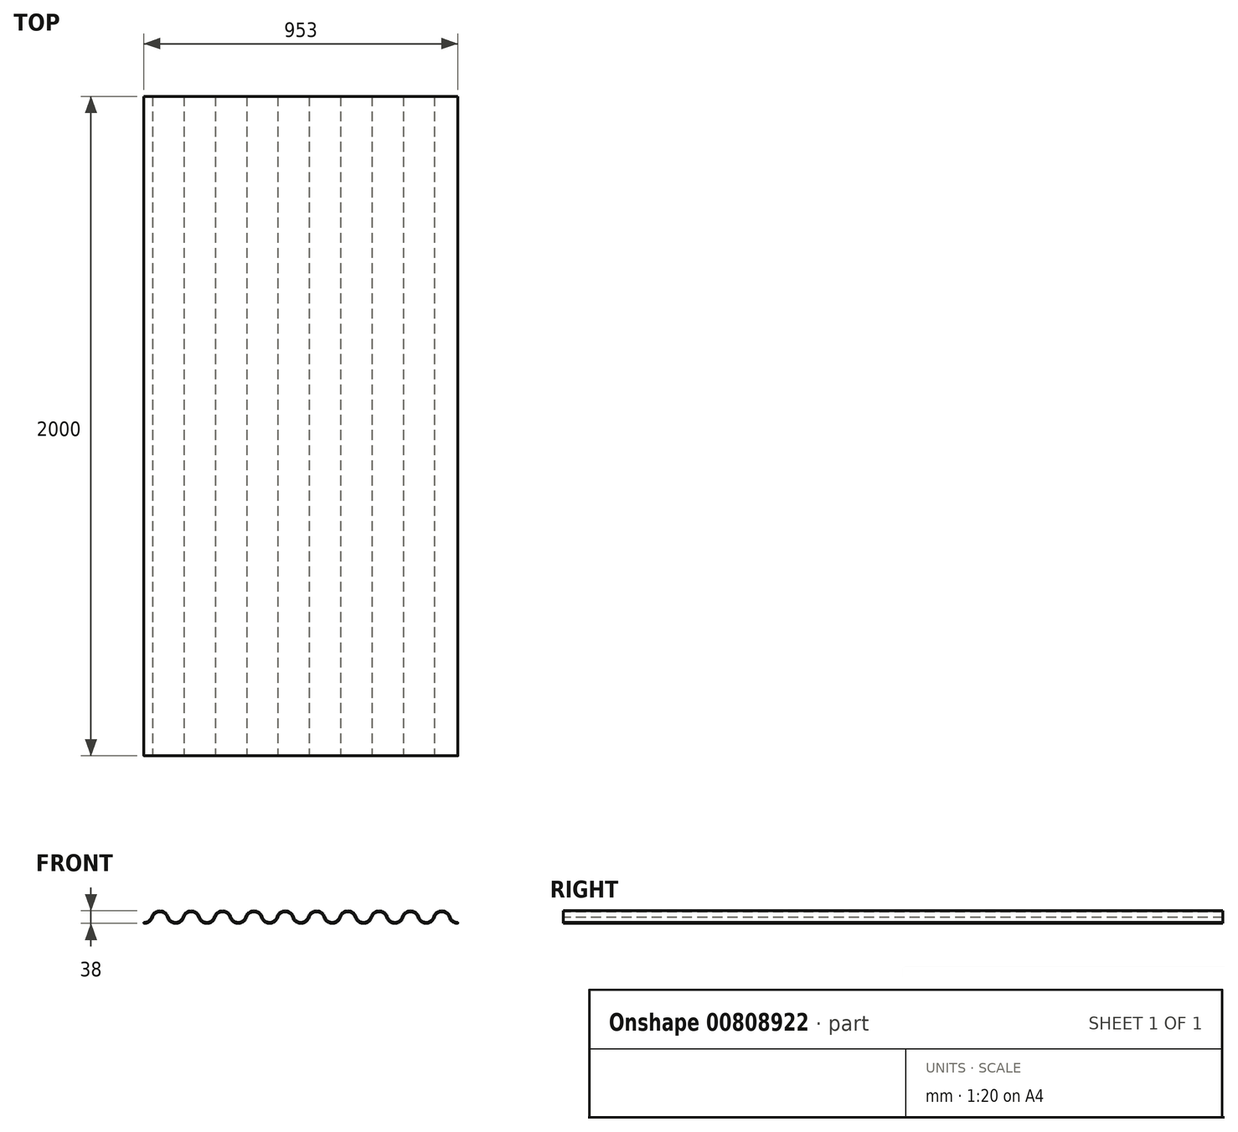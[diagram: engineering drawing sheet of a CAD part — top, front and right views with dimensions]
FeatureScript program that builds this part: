
annotation { "Feature Type Name" : "Feature", "Feature Type Description" : "" }
export const myFeature = defineFeature(function(context is Context, id is Id, definition is map)
    precondition{}
    {
        {
            var Q0;
            Q0=qCreatedBy(makeId("Front.planeOp"),FACE);
            var sketch = newSketch(context, id + "F0", { "sketchPlane" : qUnion([Q0])});
            skPoint(sketch, "E0.middle", {"position": v(0, 0) * mm});
            skArc(sketch, "E1", {"start": v(-47.5, -17.5) * mm, "mid": v(-32.61, -12.55) * mm, "end": v(-23.65, 0.32) * mm});
            skArc(sketch, "E2", {"start": v(0, 17.5) * mm, "mid": v(-14.62, 12.75) * mm, "end": v(-23.65, 0.32) * mm});
            skArc(sketch, "E3", {"start": v(23.75, 0) * mm, "mid": v(14.76, 12.66) * mm, "end": v(0, 17.5) * mm});
            skArc(sketch, "E4", {"start": v(23.75, 0) * mm, "mid": v(32.75, -12.65) * mm, "end": v(47.5, -17.5) * mm});
            skArc(sketch, "E5.0.startCap", {"start": v(-47.5, -19) * mm, "mid": v(-49, -17.5) * mm, "end": v(-47.5, -16) * mm});
            skArc(sketch, "E5.0.endCap", {"start": v(-25.1, 0.75) * mm, "mid": v(-23.23, 1.76) * mm, "end": v(-22.21, -0.1) * mm});
            skArc(sketch, "E5.0.left", {"start": v(-47.5, -16) * mm, "mid": v(-33.51, -11.35) * mm, "end": v(-25.1, 0.75) * mm});
            skArc(sketch, "E5.0.right", {"start": v(-47.5, -19) * mm, "mid": v(-31.72, -13.75) * mm, "end": v(-22.21, -0.1) * mm});
            skArc(sketch, "E5.1.startCap", {"start": v(0, 19) * mm, "mid": v(1.5, 17.5) * mm, "end": v(0, 16) * mm});
            skArc(sketch, "E5.1.endCap", {"start": v(-22.23, -0.14) * mm, "mid": v(-24.12, -1.1) * mm, "end": v(-25.08, 0.79) * mm});
            skArc(sketch, "E5.1.left", {"start": v(0, 16) * mm, "mid": v(-13.73, 11.54) * mm, "end": v(-22.23, -0.14) * mm});
            skArc(sketch, "E5.1.right", {"start": v(0, 19) * mm, "mid": v(-15.5, 13.97) * mm, "end": v(-25.08, 0.79) * mm});
            skArc(sketch, "E5.2.startCap", {"start": v(25.18, 0.44) * mm, "mid": v(24.2, -1.43) * mm, "end": v(22.32, -0.44) * mm});
            skArc(sketch, "E5.2.endCap", {"start": v(0, 16) * mm, "mid": v(-1.5, 17.5) * mm, "end": v(0, 19) * mm});
            skArc(sketch, "E5.2.left", {"start": v(22.32, -0.44) * mm, "mid": v(13.87, 11.46) * mm, "end": v(0, 16) * mm});
            skArc(sketch, "E5.2.right", {"start": v(25.18, 0.44) * mm, "mid": v(15.65, 13.87) * mm, "end": v(0, 19) * mm});
            skArc(sketch, "E5.3.startCap", {"start": v(22.32, -0.44) * mm, "mid": v(23.3, 1.43) * mm, "end": v(25.18, 0.44) * mm});
            skArc(sketch, "E5.3.endCap", {"start": v(47.5, -16) * mm, "mid": v(49, -17.5) * mm, "end": v(47.5, -19) * mm});
            skArc(sketch, "E5.3.left", {"start": v(25.18, 0.44) * mm, "mid": v(33.64, -11.44) * mm, "end": v(47.5, -16) * mm});
            skArc(sketch, "E5.3.right", {"start": v(22.32, -0.44) * mm, "mid": v(31.86, -13.86) * mm, "end": v(47.5, -19) * mm});
            skArc(sketch, "E6.1.0.0", {"start": v(47.5, -19) * mm, "mid": v(63.28, -13.75) * mm, "end": v(72.79, -0.1) * mm});
            skArc(sketch, "E6.1.0.1", {"start": v(95, 19) * mm, "mid": v(79.5, 13.97) * mm, "end": v(69.92, 0.79) * mm});
            skArc(sketch, "E6.1.0.2", {"start": v(118.75, 0) * mm, "mid": v(109.76, 12.66) * mm, "end": v(95, 17.5) * mm});
            skArc(sketch, "E6.1.0.3", {"start": v(72.77, -0.14) * mm, "mid": v(70.88, -1.1) * mm, "end": v(69.92, 0.79) * mm});
            skArc(sketch, "E6.1.0.4", {"start": v(47.5, -17.5) * mm, "mid": v(62.39, -12.55) * mm, "end": v(71.35, 0.32) * mm});
            skArc(sketch, "E6.1.0.5", {"start": v(118.75, 0) * mm, "mid": v(127.75, -12.65) * mm, "end": v(142.5, -17.5) * mm});
            skArc(sketch, "E6.1.0.6", {"start": v(95, 17.5) * mm, "mid": v(80.38, 12.75) * mm, "end": v(71.35, 0.32) * mm});
            skPoint(sketch, "E6.1.0.7", {"position": v(95, 0) * mm});
            skArc(sketch, "E6.1.0.8", {"start": v(95, 16) * mm, "mid": v(81.27, 11.54) * mm, "end": v(72.77, -0.14) * mm});
            skArc(sketch, "E6.1.0.9", {"start": v(117.32, -0.44) * mm, "mid": v(108.87, 11.46) * mm, "end": v(95, 16) * mm});
            skArc(sketch, "E6.1.0.10", {"start": v(120.18, 0.44) * mm, "mid": v(128.64, -11.44) * mm, "end": v(142.5, -16) * mm});
            skArc(sketch, "E6.1.0.11", {"start": v(95, 19) * mm, "mid": v(96.5, 17.5) * mm, "end": v(95, 16) * mm});
            skArc(sketch, "E6.1.0.12", {"start": v(47.5, -16) * mm, "mid": v(61.49, -11.35) * mm, "end": v(69.9, 0.75) * mm});
            skArc(sketch, "E6.1.0.13", {"start": v(117.32, -0.44) * mm, "mid": v(126.86, -13.86) * mm, "end": v(142.5, -19) * mm});
            skArc(sketch, "E6.1.0.14", {"start": v(120.18, 0.44) * mm, "mid": v(119.2, -1.43) * mm, "end": v(117.32, -0.44) * mm});
            skArc(sketch, "E6.1.0.15", {"start": v(47.5, -19) * mm, "mid": v(46, -17.5) * mm, "end": v(47.5, -16) * mm});
            skArc(sketch, "E6.1.0.16", {"start": v(69.9, 0.75) * mm, "mid": v(71.77, 1.76) * mm, "end": v(72.79, -0.1) * mm});
            skArc(sketch, "E6.1.0.17", {"start": v(142.5, -16) * mm, "mid": v(144, -17.5) * mm, "end": v(142.5, -19) * mm});
            skArc(sketch, "E6.1.0.18", {"start": v(120.18, 0.44) * mm, "mid": v(110.65, 13.87) * mm, "end": v(95, 19) * mm});
            skArc(sketch, "E6.1.0.19", {"start": v(117.32, -0.44) * mm, "mid": v(118.3, 1.43) * mm, "end": v(120.18, 0.44) * mm});
            skArc(sketch, "E6.1.0.20", {"start": v(95, 16) * mm, "mid": v(93.5, 17.5) * mm, "end": v(95, 19) * mm});
            skArc(sketch, "E6.2.0.0", {"start": v(142.5, -19) * mm, "mid": v(158.28, -13.75) * mm, "end": v(167.79, -0.1) * mm});
            skArc(sketch, "E6.2.0.1", {"start": v(190, 19) * mm, "mid": v(174.5, 13.97) * mm, "end": v(164.92, 0.79) * mm});
            skArc(sketch, "E6.2.0.2", {"start": v(213.75, 0) * mm, "mid": v(204.76, 12.66) * mm, "end": v(190, 17.5) * mm});
            skArc(sketch, "E6.2.0.3", {"start": v(167.77, -0.14) * mm, "mid": v(165.88, -1.1) * mm, "end": v(164.92, 0.79) * mm});
            skArc(sketch, "E6.2.0.4", {"start": v(142.5, -17.5) * mm, "mid": v(157.39, -12.55) * mm, "end": v(166.35, 0.32) * mm});
            skArc(sketch, "E6.2.0.5", {"start": v(213.75, 0) * mm, "mid": v(222.75, -12.65) * mm, "end": v(237.5, -17.5) * mm});
            skArc(sketch, "E6.2.0.6", {"start": v(190, 17.5) * mm, "mid": v(175.38, 12.75) * mm, "end": v(166.35, 0.32) * mm});
            skPoint(sketch, "E6.2.0.7", {"position": v(190, 0) * mm});
            skArc(sketch, "E6.2.0.8", {"start": v(190, 16) * mm, "mid": v(176.27, 11.54) * mm, "end": v(167.77, -0.14) * mm});
            skArc(sketch, "E6.2.0.9", {"start": v(212.32, -0.44) * mm, "mid": v(203.87, 11.46) * mm, "end": v(190, 16) * mm});
            skArc(sketch, "E6.2.0.10", {"start": v(215.18, 0.44) * mm, "mid": v(223.64, -11.44) * mm, "end": v(237.5, -16) * mm});
            skArc(sketch, "E6.2.0.11", {"start": v(190, 19) * mm, "mid": v(191.5, 17.5) * mm, "end": v(190, 16) * mm});
            skArc(sketch, "E6.2.0.12", {"start": v(142.5, -16) * mm, "mid": v(156.49, -11.35) * mm, "end": v(164.9, 0.75) * mm});
            skArc(sketch, "E6.2.0.13", {"start": v(212.32, -0.44) * mm, "mid": v(221.86, -13.86) * mm, "end": v(237.5, -19) * mm});
            skArc(sketch, "E6.2.0.14", {"start": v(215.18, 0.44) * mm, "mid": v(214.2, -1.43) * mm, "end": v(212.32, -0.44) * mm});
            skArc(sketch, "E6.2.0.15", {"start": v(142.5, -19) * mm, "mid": v(141, -17.5) * mm, "end": v(142.5, -16) * mm});
            skArc(sketch, "E6.2.0.16", {"start": v(164.9, 0.75) * mm, "mid": v(166.77, 1.76) * mm, "end": v(167.79, -0.1) * mm});
            skArc(sketch, "E6.2.0.17", {"start": v(237.5, -16) * mm, "mid": v(239, -17.5) * mm, "end": v(237.5, -19) * mm});
            skArc(sketch, "E6.2.0.18", {"start": v(215.18, 0.44) * mm, "mid": v(205.65, 13.87) * mm, "end": v(190, 19) * mm});
            skArc(sketch, "E6.2.0.19", {"start": v(212.32, -0.44) * mm, "mid": v(213.3, 1.43) * mm, "end": v(215.18, 0.44) * mm});
            skArc(sketch, "E6.2.0.20", {"start": v(190, 16) * mm, "mid": v(188.5, 17.5) * mm, "end": v(190, 19) * mm});
            skArc(sketch, "E6.3.0.0", {"start": v(237.5, -19) * mm, "mid": v(253.28, -13.75) * mm, "end": v(262.79, -0.1) * mm});
            skArc(sketch, "E6.3.0.1", {"start": v(285, 19) * mm, "mid": v(269.5, 13.97) * mm, "end": v(259.92, 0.79) * mm});
            skArc(sketch, "E6.3.0.2", {"start": v(308.75, 0) * mm, "mid": v(299.76, 12.66) * mm, "end": v(285, 17.5) * mm});
            skArc(sketch, "E6.3.0.3", {"start": v(262.77, -0.14) * mm, "mid": v(260.88, -1.1) * mm, "end": v(259.92, 0.79) * mm});
            skArc(sketch, "E6.3.0.4", {"start": v(237.5, -17.5) * mm, "mid": v(252.39, -12.55) * mm, "end": v(261.35, 0.32) * mm});
            skArc(sketch, "E6.3.0.5", {"start": v(308.75, 0) * mm, "mid": v(317.75, -12.65) * mm, "end": v(332.5, -17.5) * mm});
            skArc(sketch, "E6.3.0.6", {"start": v(285, 17.5) * mm, "mid": v(270.38, 12.75) * mm, "end": v(261.35, 0.32) * mm});
            skPoint(sketch, "E6.3.0.7", {"position": v(285, 0) * mm});
            skArc(sketch, "E6.3.0.8", {"start": v(285, 16) * mm, "mid": v(271.27, 11.54) * mm, "end": v(262.77, -0.14) * mm});
            skArc(sketch, "E6.3.0.9", {"start": v(307.32, -0.44) * mm, "mid": v(298.87, 11.46) * mm, "end": v(285, 16) * mm});
            skArc(sketch, "E6.3.0.10", {"start": v(310.18, 0.44) * mm, "mid": v(318.64, -11.44) * mm, "end": v(332.5, -16) * mm});
            skArc(sketch, "E6.3.0.11", {"start": v(285, 19) * mm, "mid": v(286.5, 17.5) * mm, "end": v(285, 16) * mm});
            skArc(sketch, "E6.3.0.12", {"start": v(237.5, -16) * mm, "mid": v(251.49, -11.35) * mm, "end": v(259.9, 0.75) * mm});
            skArc(sketch, "E6.3.0.13", {"start": v(307.32, -0.44) * mm, "mid": v(316.86, -13.86) * mm, "end": v(332.5, -19) * mm});
            skArc(sketch, "E6.3.0.14", {"start": v(310.18, 0.44) * mm, "mid": v(309.2, -1.43) * mm, "end": v(307.32, -0.44) * mm});
            skArc(sketch, "E6.3.0.15", {"start": v(237.5, -19) * mm, "mid": v(236, -17.5) * mm, "end": v(237.5, -16) * mm});
            skArc(sketch, "E6.3.0.16", {"start": v(259.9, 0.75) * mm, "mid": v(261.77, 1.76) * mm, "end": v(262.79, -0.1) * mm});
            skArc(sketch, "E6.3.0.17", {"start": v(332.5, -16) * mm, "mid": v(334, -17.5) * mm, "end": v(332.5, -19) * mm});
            skArc(sketch, "E6.3.0.18", {"start": v(310.18, 0.44) * mm, "mid": v(300.65, 13.87) * mm, "end": v(285, 19) * mm});
            skArc(sketch, "E6.3.0.19", {"start": v(307.32, -0.44) * mm, "mid": v(308.3, 1.43) * mm, "end": v(310.18, 0.44) * mm});
            skArc(sketch, "E6.3.0.20", {"start": v(285, 16) * mm, "mid": v(283.5, 17.5) * mm, "end": v(285, 19) * mm});
            skArc(sketch, "E6.4.0.0", {"start": v(332.5, -19) * mm, "mid": v(348.28, -13.75) * mm, "end": v(357.79, -0.1) * mm});
            skArc(sketch, "E6.4.0.1", {"start": v(380, 19) * mm, "mid": v(364.5, 13.97) * mm, "end": v(354.92, 0.79) * mm});
            skArc(sketch, "E6.4.0.2", {"start": v(403.75, 0) * mm, "mid": v(394.76, 12.66) * mm, "end": v(380, 17.5) * mm});
            skArc(sketch, "E6.4.0.3", {"start": v(357.77, -0.14) * mm, "mid": v(355.88, -1.1) * mm, "end": v(354.92, 0.79) * mm});
            skArc(sketch, "E6.4.0.4", {"start": v(332.5, -17.5) * mm, "mid": v(347.39, -12.55) * mm, "end": v(356.35, 0.32) * mm});
            skArc(sketch, "E6.4.0.5", {"start": v(403.75, 0) * mm, "mid": v(412.75, -12.65) * mm, "end": v(427.5, -17.5) * mm});
            skArc(sketch, "E6.4.0.6", {"start": v(380, 17.5) * mm, "mid": v(365.38, 12.75) * mm, "end": v(356.35, 0.32) * mm});
            skPoint(sketch, "E6.4.0.7", {"position": v(380, 0) * mm});
            skArc(sketch, "E6.4.0.8", {"start": v(380, 16) * mm, "mid": v(366.27, 11.54) * mm, "end": v(357.77, -0.14) * mm});
            skArc(sketch, "E6.4.0.9", {"start": v(402.32, -0.44) * mm, "mid": v(393.87, 11.46) * mm, "end": v(380, 16) * mm});
            skArc(sketch, "E6.4.0.10", {"start": v(405.18, 0.44) * mm, "mid": v(413.64, -11.44) * mm, "end": v(427.5, -16) * mm});
            skArc(sketch, "E6.4.0.11", {"start": v(380, 19) * mm, "mid": v(381.5, 17.5) * mm, "end": v(380, 16) * mm});
            skArc(sketch, "E6.4.0.12", {"start": v(332.5, -16) * mm, "mid": v(346.49, -11.35) * mm, "end": v(354.9, 0.75) * mm});
            skArc(sketch, "E6.4.0.13", {"start": v(402.32, -0.44) * mm, "mid": v(411.86, -13.86) * mm, "end": v(427.5, -19) * mm});
            skArc(sketch, "E6.4.0.14", {"start": v(405.18, 0.44) * mm, "mid": v(404.2, -1.43) * mm, "end": v(402.32, -0.44) * mm});
            skArc(sketch, "E6.4.0.15", {"start": v(332.5, -19) * mm, "mid": v(331, -17.5) * mm, "end": v(332.5, -16) * mm});
            skArc(sketch, "E6.4.0.16", {"start": v(354.9, 0.75) * mm, "mid": v(356.77, 1.76) * mm, "end": v(357.79, -0.1) * mm});
            skArc(sketch, "E6.4.0.17", {"start": v(427.5, -16) * mm, "mid": v(429, -17.5) * mm, "end": v(427.5, -19) * mm});
            skArc(sketch, "E6.4.0.18", {"start": v(405.18, 0.44) * mm, "mid": v(395.65, 13.87) * mm, "end": v(380, 19) * mm});
            skArc(sketch, "E6.4.0.19", {"start": v(402.32, -0.44) * mm, "mid": v(403.3, 1.43) * mm, "end": v(405.18, 0.44) * mm});
            skArc(sketch, "E6.4.0.20", {"start": v(380, 16) * mm, "mid": v(378.5, 17.5) * mm, "end": v(380, 19) * mm});
            skArc(sketch, "E6.5.0.0", {"start": v(427.5, -19) * mm, "mid": v(443.28, -13.75) * mm, "end": v(452.79, -0.1) * mm});
            skArc(sketch, "E6.5.0.1", {"start": v(475, 19) * mm, "mid": v(459.5, 13.97) * mm, "end": v(449.92, 0.79) * mm});
            skArc(sketch, "E6.5.0.2", {"start": v(498.75, 0) * mm, "mid": v(489.76, 12.66) * mm, "end": v(475, 17.5) * mm});
            skArc(sketch, "E6.5.0.3", {"start": v(452.77, -0.14) * mm, "mid": v(450.88, -1.1) * mm, "end": v(449.92, 0.79) * mm});
            skArc(sketch, "E6.5.0.4", {"start": v(427.5, -17.5) * mm, "mid": v(442.39, -12.55) * mm, "end": v(451.35, 0.32) * mm});
            skArc(sketch, "E6.5.0.5", {"start": v(498.75, 0) * mm, "mid": v(507.75, -12.65) * mm, "end": v(522.5, -17.5) * mm});
            skArc(sketch, "E6.5.0.6", {"start": v(475, 17.5) * mm, "mid": v(460.38, 12.75) * mm, "end": v(451.35, 0.32) * mm});
            skPoint(sketch, "E6.5.0.7", {"position": v(475, 0) * mm});
            skArc(sketch, "E6.5.0.8", {"start": v(475, 16) * mm, "mid": v(461.27, 11.54) * mm, "end": v(452.77, -0.14) * mm});
            skArc(sketch, "E6.5.0.9", {"start": v(497.32, -0.44) * mm, "mid": v(488.87, 11.46) * mm, "end": v(475, 16) * mm});
            skArc(sketch, "E6.5.0.10", {"start": v(500.18, 0.44) * mm, "mid": v(508.64, -11.44) * mm, "end": v(522.5, -16) * mm});
            skArc(sketch, "E6.5.0.11", {"start": v(475, 19) * mm, "mid": v(476.5, 17.5) * mm, "end": v(475, 16) * mm});
            skArc(sketch, "E6.5.0.12", {"start": v(427.5, -16) * mm, "mid": v(441.49, -11.35) * mm, "end": v(449.9, 0.75) * mm});
            skArc(sketch, "E6.5.0.13", {"start": v(497.32, -0.44) * mm, "mid": v(506.86, -13.86) * mm, "end": v(522.5, -19) * mm});
            skArc(sketch, "E6.5.0.14", {"start": v(500.18, 0.44) * mm, "mid": v(499.2, -1.43) * mm, "end": v(497.32, -0.44) * mm});
            skArc(sketch, "E6.5.0.15", {"start": v(427.5, -19) * mm, "mid": v(426, -17.5) * mm, "end": v(427.5, -16) * mm});
            skArc(sketch, "E6.5.0.16", {"start": v(449.9, 0.75) * mm, "mid": v(451.77, 1.76) * mm, "end": v(452.79, -0.1) * mm});
            skArc(sketch, "E6.5.0.17", {"start": v(522.5, -16) * mm, "mid": v(524, -17.5) * mm, "end": v(522.5, -19) * mm});
            skArc(sketch, "E6.5.0.18", {"start": v(500.18, 0.44) * mm, "mid": v(490.65, 13.87) * mm, "end": v(475, 19) * mm});
            skArc(sketch, "E6.5.0.19", {"start": v(497.32, -0.44) * mm, "mid": v(498.3, 1.43) * mm, "end": v(500.18, 0.44) * mm});
            skArc(sketch, "E6.5.0.20", {"start": v(475, 16) * mm, "mid": v(473.5, 17.5) * mm, "end": v(475, 19) * mm});
            skArc(sketch, "E6.6.0.0", {"start": v(522.5, -19) * mm, "mid": v(538.28, -13.75) * mm, "end": v(547.79, -0.1) * mm});
            skArc(sketch, "E6.6.0.1", {"start": v(570, 19) * mm, "mid": v(554.5, 13.97) * mm, "end": v(544.92, 0.79) * mm});
            skArc(sketch, "E6.6.0.2", {"start": v(593.75, 0) * mm, "mid": v(584.76, 12.66) * mm, "end": v(570, 17.5) * mm});
            skArc(sketch, "E6.6.0.3", {"start": v(547.77, -0.14) * mm, "mid": v(545.88, -1.1) * mm, "end": v(544.92, 0.79) * mm});
            skArc(sketch, "E6.6.0.4", {"start": v(522.5, -17.5) * mm, "mid": v(537.39, -12.55) * mm, "end": v(546.35, 0.32) * mm});
            skArc(sketch, "E6.6.0.5", {"start": v(593.75, 0) * mm, "mid": v(602.75, -12.65) * mm, "end": v(617.5, -17.5) * mm});
            skArc(sketch, "E6.6.0.6", {"start": v(570, 17.5) * mm, "mid": v(555.38, 12.75) * mm, "end": v(546.35, 0.32) * mm});
            skPoint(sketch, "E6.6.0.7", {"position": v(570, 0) * mm});
            skArc(sketch, "E6.6.0.8", {"start": v(570, 16) * mm, "mid": v(556.27, 11.54) * mm, "end": v(547.77, -0.14) * mm});
            skArc(sketch, "E6.6.0.9", {"start": v(592.32, -0.44) * mm, "mid": v(583.87, 11.46) * mm, "end": v(570, 16) * mm});
            skArc(sketch, "E6.6.0.10", {"start": v(595.18, 0.44) * mm, "mid": v(603.64, -11.44) * mm, "end": v(617.5, -16) * mm});
            skArc(sketch, "E6.6.0.11", {"start": v(570, 19) * mm, "mid": v(571.5, 17.5) * mm, "end": v(570, 16) * mm});
            skArc(sketch, "E6.6.0.12", {"start": v(522.5, -16) * mm, "mid": v(536.49, -11.35) * mm, "end": v(544.9, 0.75) * mm});
            skArc(sketch, "E6.6.0.13", {"start": v(592.32, -0.44) * mm, "mid": v(601.86, -13.86) * mm, "end": v(617.5, -19) * mm});
            skArc(sketch, "E6.6.0.14", {"start": v(595.18, 0.44) * mm, "mid": v(594.2, -1.43) * mm, "end": v(592.32, -0.44) * mm});
            skArc(sketch, "E6.6.0.15", {"start": v(522.5, -19) * mm, "mid": v(521, -17.5) * mm, "end": v(522.5, -16) * mm});
            skArc(sketch, "E6.6.0.16", {"start": v(544.9, 0.75) * mm, "mid": v(546.77, 1.76) * mm, "end": v(547.79, -0.1) * mm});
            skArc(sketch, "E6.6.0.17", {"start": v(617.5, -16) * mm, "mid": v(619, -17.5) * mm, "end": v(617.5, -19) * mm});
            skArc(sketch, "E6.6.0.18", {"start": v(595.18, 0.44) * mm, "mid": v(585.65, 13.87) * mm, "end": v(570, 19) * mm});
            skArc(sketch, "E6.6.0.19", {"start": v(592.32, -0.44) * mm, "mid": v(593.3, 1.43) * mm, "end": v(595.18, 0.44) * mm});
            skArc(sketch, "E6.6.0.20", {"start": v(570, 16) * mm, "mid": v(568.5, 17.5) * mm, "end": v(570, 19) * mm});
            skArc(sketch, "E6.7.0.0", {"start": v(617.5, -19) * mm, "mid": v(633.28, -13.75) * mm, "end": v(642.79, -0.1) * mm});
            skArc(sketch, "E6.7.0.1", {"start": v(665, 19) * mm, "mid": v(649.5, 13.97) * mm, "end": v(639.92, 0.79) * mm});
            skArc(sketch, "E6.7.0.2", {"start": v(688.75, 0) * mm, "mid": v(679.76, 12.66) * mm, "end": v(665, 17.5) * mm});
            skArc(sketch, "E6.7.0.3", {"start": v(642.77, -0.14) * mm, "mid": v(640.88, -1.1) * mm, "end": v(639.92, 0.79) * mm});
            skArc(sketch, "E6.7.0.4", {"start": v(617.5, -17.5) * mm, "mid": v(632.39, -12.55) * mm, "end": v(641.35, 0.32) * mm});
            skArc(sketch, "E6.7.0.5", {"start": v(688.75, 0) * mm, "mid": v(697.75, -12.65) * mm, "end": v(712.5, -17.5) * mm});
            skArc(sketch, "E6.7.0.6", {"start": v(665, 17.5) * mm, "mid": v(650.38, 12.75) * mm, "end": v(641.35, 0.32) * mm});
            skPoint(sketch, "E6.7.0.7", {"position": v(665, 0) * mm});
            skArc(sketch, "E6.7.0.8", {"start": v(665, 16) * mm, "mid": v(651.27, 11.54) * mm, "end": v(642.77, -0.14) * mm});
            skArc(sketch, "E6.7.0.9", {"start": v(687.32, -0.44) * mm, "mid": v(678.87, 11.46) * mm, "end": v(665, 16) * mm});
            skArc(sketch, "E6.7.0.10", {"start": v(690.18, 0.44) * mm, "mid": v(698.64, -11.44) * mm, "end": v(712.5, -16) * mm});
            skArc(sketch, "E6.7.0.11", {"start": v(665, 19) * mm, "mid": v(666.5, 17.5) * mm, "end": v(665, 16) * mm});
            skArc(sketch, "E6.7.0.12", {"start": v(617.5, -16) * mm, "mid": v(631.49, -11.35) * mm, "end": v(639.9, 0.75) * mm});
            skArc(sketch, "E6.7.0.13", {"start": v(687.32, -0.44) * mm, "mid": v(696.86, -13.86) * mm, "end": v(712.5, -19) * mm});
            skArc(sketch, "E6.7.0.14", {"start": v(690.18, 0.44) * mm, "mid": v(689.2, -1.43) * mm, "end": v(687.32, -0.44) * mm});
            skArc(sketch, "E6.7.0.15", {"start": v(617.5, -19) * mm, "mid": v(616, -17.5) * mm, "end": v(617.5, -16) * mm});
            skArc(sketch, "E6.7.0.16", {"start": v(639.9, 0.75) * mm, "mid": v(641.77, 1.76) * mm, "end": v(642.79, -0.1) * mm});
            skArc(sketch, "E6.7.0.17", {"start": v(712.5, -16) * mm, "mid": v(714, -17.5) * mm, "end": v(712.5, -19) * mm});
            skArc(sketch, "E6.7.0.18", {"start": v(690.18, 0.44) * mm, "mid": v(680.65, 13.87) * mm, "end": v(665, 19) * mm});
            skArc(sketch, "E6.7.0.19", {"start": v(687.32, -0.44) * mm, "mid": v(688.3, 1.43) * mm, "end": v(690.18, 0.44) * mm});
            skArc(sketch, "E6.7.0.20", {"start": v(665, 16) * mm, "mid": v(663.5, 17.5) * mm, "end": v(665, 19) * mm});
            skArc(sketch, "E6.8.0.0", {"start": v(712.5, -19) * mm, "mid": v(728.28, -13.75) * mm, "end": v(737.79, -0.1) * mm});
            skArc(sketch, "E6.8.0.1", {"start": v(760, 19) * mm, "mid": v(744.5, 13.97) * mm, "end": v(734.92, 0.79) * mm});
            skArc(sketch, "E6.8.0.2", {"start": v(783.75, 0) * mm, "mid": v(774.76, 12.66) * mm, "end": v(760, 17.5) * mm});
            skArc(sketch, "E6.8.0.3", {"start": v(737.77, -0.14) * mm, "mid": v(735.88, -1.1) * mm, "end": v(734.92, 0.79) * mm});
            skArc(sketch, "E6.8.0.4", {"start": v(712.5, -17.5) * mm, "mid": v(727.39, -12.55) * mm, "end": v(736.35, 0.32) * mm});
            skArc(sketch, "E6.8.0.5", {"start": v(783.75, 0) * mm, "mid": v(792.75, -12.65) * mm, "end": v(807.5, -17.5) * mm});
            skArc(sketch, "E6.8.0.6", {"start": v(760, 17.5) * mm, "mid": v(745.38, 12.75) * mm, "end": v(736.35, 0.32) * mm});
            skPoint(sketch, "E6.8.0.7", {"position": v(760, 0) * mm});
            skArc(sketch, "E6.8.0.8", {"start": v(760, 16) * mm, "mid": v(746.27, 11.54) * mm, "end": v(737.77, -0.14) * mm});
            skArc(sketch, "E6.8.0.9", {"start": v(782.32, -0.44) * mm, "mid": v(773.87, 11.46) * mm, "end": v(760, 16) * mm});
            skArc(sketch, "E6.8.0.10", {"start": v(785.18, 0.44) * mm, "mid": v(793.64, -11.44) * mm, "end": v(807.5, -16) * mm});
            skArc(sketch, "E6.8.0.11", {"start": v(760, 19) * mm, "mid": v(761.5, 17.5) * mm, "end": v(760, 16) * mm});
            skArc(sketch, "E6.8.0.12", {"start": v(712.5, -16) * mm, "mid": v(726.49, -11.35) * mm, "end": v(734.9, 0.75) * mm});
            skArc(sketch, "E6.8.0.13", {"start": v(782.32, -0.44) * mm, "mid": v(791.86, -13.86) * mm, "end": v(807.5, -19) * mm});
            skArc(sketch, "E6.8.0.14", {"start": v(785.18, 0.44) * mm, "mid": v(784.2, -1.43) * mm, "end": v(782.32, -0.44) * mm});
            skArc(sketch, "E6.8.0.15", {"start": v(712.5, -19) * mm, "mid": v(711, -17.5) * mm, "end": v(712.5, -16) * mm});
            skArc(sketch, "E6.8.0.16", {"start": v(734.9, 0.75) * mm, "mid": v(736.77, 1.76) * mm, "end": v(737.79, -0.1) * mm});
            skArc(sketch, "E6.8.0.17", {"start": v(807.5, -16) * mm, "mid": v(809, -17.5) * mm, "end": v(807.5, -19) * mm});
            skArc(sketch, "E6.8.0.18", {"start": v(785.18, 0.44) * mm, "mid": v(775.65, 13.87) * mm, "end": v(760, 19) * mm});
            skArc(sketch, "E6.8.0.19", {"start": v(782.32, -0.44) * mm, "mid": v(783.3, 1.43) * mm, "end": v(785.18, 0.44) * mm});
            skArc(sketch, "E6.8.0.20", {"start": v(760, 16) * mm, "mid": v(758.5, 17.5) * mm, "end": v(760, 19) * mm});
            skArc(sketch, "E6.9.0.0", {"start": v(807.5, -19) * mm, "mid": v(823.28, -13.75) * mm, "end": v(832.79, -0.1) * mm});
            skArc(sketch, "E6.9.0.1", {"start": v(855, 19) * mm, "mid": v(839.5, 13.97) * mm, "end": v(829.92, 0.79) * mm});
            skArc(sketch, "E6.9.0.2", {"start": v(878.75, 0) * mm, "mid": v(869.76, 12.66) * mm, "end": v(855, 17.5) * mm});
            skArc(sketch, "E6.9.0.3", {"start": v(832.77, -0.14) * mm, "mid": v(830.88, -1.1) * mm, "end": v(829.92, 0.79) * mm});
            skArc(sketch, "E6.9.0.4", {"start": v(807.5, -17.5) * mm, "mid": v(822.39, -12.55) * mm, "end": v(831.35, 0.32) * mm});
            skArc(sketch, "E6.9.0.5", {"start": v(878.75, 0) * mm, "mid": v(887.75, -12.65) * mm, "end": v(902.5, -17.5) * mm});
            skArc(sketch, "E6.9.0.6", {"start": v(855, 17.5) * mm, "mid": v(840.38, 12.75) * mm, "end": v(831.35, 0.32) * mm});
            skPoint(sketch, "E6.9.0.7", {"position": v(855, 0) * mm});
            skArc(sketch, "E6.9.0.8", {"start": v(855, 16) * mm, "mid": v(841.27, 11.54) * mm, "end": v(832.77, -0.14) * mm});
            skArc(sketch, "E6.9.0.9", {"start": v(877.32, -0.44) * mm, "mid": v(868.87, 11.46) * mm, "end": v(855, 16) * mm});
            skArc(sketch, "E6.9.0.10", {"start": v(880.18, 0.44) * mm, "mid": v(888.64, -11.44) * mm, "end": v(902.5, -16) * mm});
            skArc(sketch, "E6.9.0.11", {"start": v(855, 19) * mm, "mid": v(856.5, 17.5) * mm, "end": v(855, 16) * mm});
            skArc(sketch, "E6.9.0.12", {"start": v(807.5, -16) * mm, "mid": v(821.49, -11.35) * mm, "end": v(829.9, 0.75) * mm});
            skArc(sketch, "E6.9.0.13", {"start": v(877.32, -0.44) * mm, "mid": v(886.86, -13.86) * mm, "end": v(902.5, -19) * mm});
            skArc(sketch, "E6.9.0.14", {"start": v(880.18, 0.44) * mm, "mid": v(879.2, -1.43) * mm, "end": v(877.32, -0.44) * mm});
            skArc(sketch, "E6.9.0.15", {"start": v(807.5, -19) * mm, "mid": v(806, -17.5) * mm, "end": v(807.5, -16) * mm});
            skArc(sketch, "E6.9.0.16", {"start": v(829.9, 0.75) * mm, "mid": v(831.77, 1.76) * mm, "end": v(832.79, -0.1) * mm});
            skArc(sketch, "E6.9.0.17", {"start": v(902.5, -16) * mm, "mid": v(904, -17.5) * mm, "end": v(902.5, -19) * mm});
            skArc(sketch, "E6.9.0.18", {"start": v(880.18, 0.44) * mm, "mid": v(870.65, 13.87) * mm, "end": v(855, 19) * mm});
            skArc(sketch, "E6.9.0.19", {"start": v(877.32, -0.44) * mm, "mid": v(878.3, 1.43) * mm, "end": v(880.18, 0.44) * mm});
            skArc(sketch, "E6.9.0.20", {"start": v(855, 16) * mm, "mid": v(853.5, 17.5) * mm, "end": v(855, 19) * mm});
            skLineSegment(sketch, "E6.direction1", {"start": v(-47.5, -19) * mm, "end": v(47.5, -19) * mm, "construction": true});
            skSolve(sketch);
        }
        {
            var Q0;
            Q0 = qSketchRegion(id + "F0", true);
            extrude(context, id + "F1", {"entities" : qUnion([Q0]), "oppositeDirection" : true, "depth" : 2000 * mm, "offsetDistance" : 25 * mm});
        }
    });
